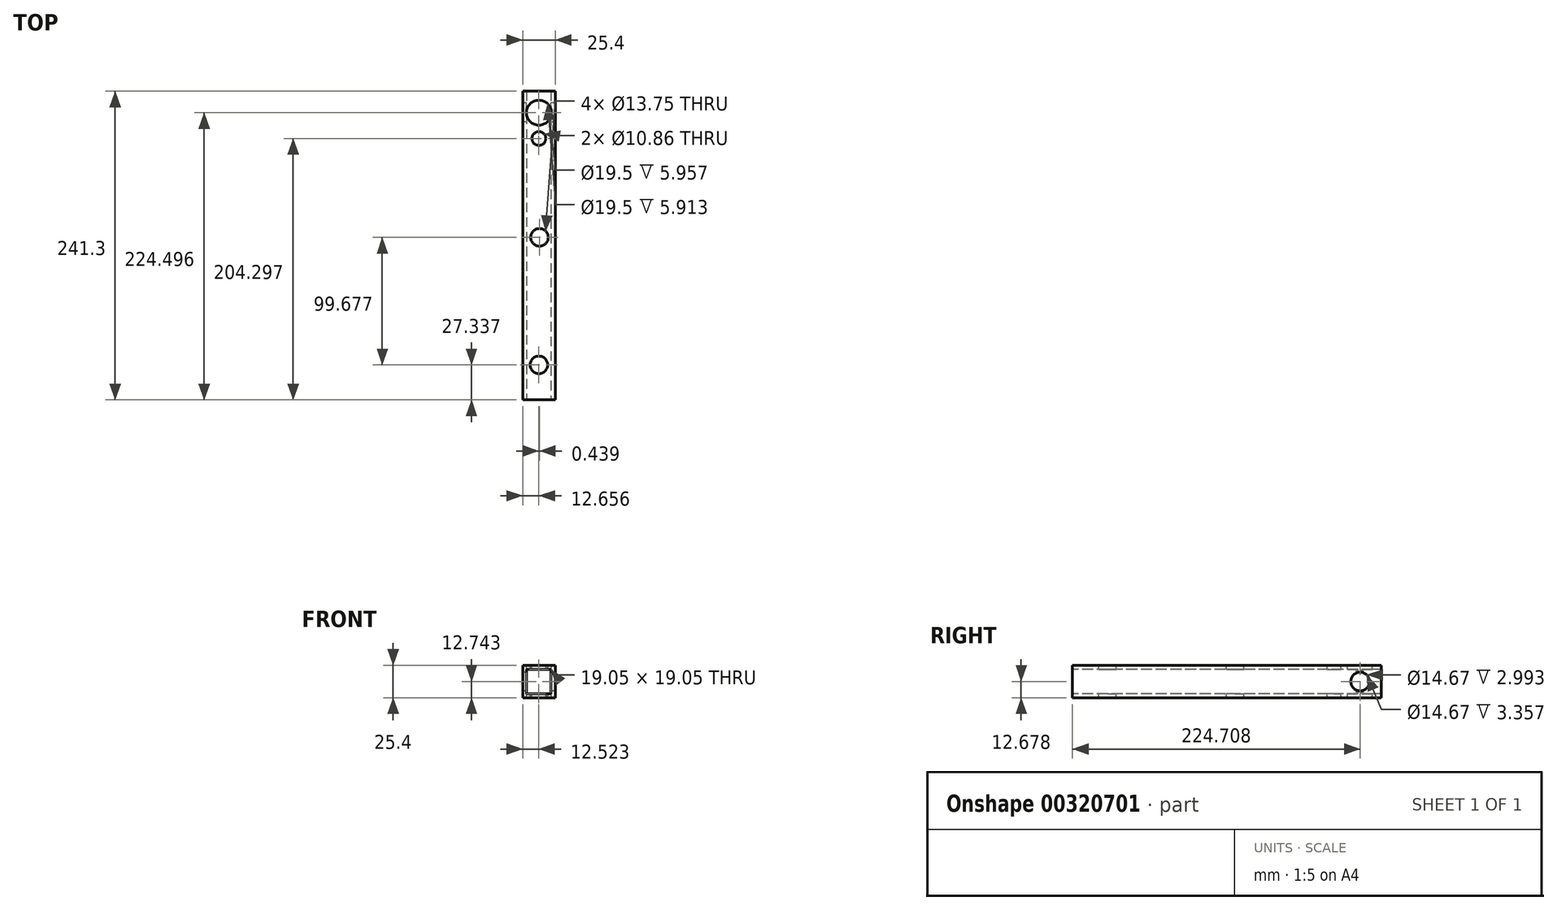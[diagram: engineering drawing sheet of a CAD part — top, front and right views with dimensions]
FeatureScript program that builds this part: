
annotation { "Feature Type Name" : "Feature", "Feature Type Description" : "" }
export const myFeature = defineFeature(function(context is Context, id is Id, definition is map)
    precondition{}
    {
        {
            var Q0;
            Q0=qCreatedBy(makeId("Top.planeOp"),FACE);
            var sketch = newSketch(context, id + "F0", { "sketchPlane" : qUnion([Q0])});
            skLineSegment(sketch, "E0", {"start": v(-60.08, 121.67) * mm, "end": v(-60.08, -119.63) * mm});
            skLineSegment(sketch, "E1", {"start": v(-60.08, -119.63) * mm, "end": v(-34.68, -119.63) * mm});
            skLineSegment(sketch, "E2", {"start": v(-34.68, -119.63) * mm, "end": v(-34.68, 121.67) * mm});
            skLineSegment(sketch, "E3", {"start": v(-34.68, 121.67) * mm, "end": v(-60.08, 121.67) * mm});
            skSolve(sketch);
        }
        {
            var Q0;
            Q0=makeQuery(id+"F0.imprint","IMPRINT",FACE,{"disambiguationData":[TD([[makeQuery(id+"F0.imprint","IMPRINT",EDGE,{"derivedFrom":sQuery(id+"F0.wireOp",EDGE,"E0")}),1.0]])]});
            extrude(context, id + "F1", {"entities" : qUnion([Q0]), "depth" : 25.4 * mm});
        }
        {
            var Q0;
            Q0=makeQuery(id+"F1.opExtrude","SWEPT_FACE",FACE,{"disambiguationData":[OSD([sQuery(id+"F0.wireOp",EDGE,"E1")])]});
            var sketch = newSketch(context, id + "F2", { "sketchPlane" : qUnion([Q0])});
            skLineSegment(sketch, "E4", {"start": v(-57.08, 22.27) * mm, "end": v(-57.08, 3.22) * mm});
            skLineSegment(sketch, "E5", {"start": v(-57.08, 3.22) * mm, "end": v(-38.03, 3.22) * mm});
            skLineSegment(sketch, "E6", {"start": v(-38.03, 3.22) * mm, "end": v(-38.03, 22.27) * mm});
            skLineSegment(sketch, "E7", {"start": v(-38.03, 22.27) * mm, "end": v(-57.08, 22.27) * mm});
            skSolve(sketch);
        }
        {
            var Q0;
            Q0=qSketchRegion(id+"F2",true);
            extrude(context, id + "F3", {"entities" : qUnion([Q0]), "operationType" : NewBodyOperationType.REMOVE, "oppositeDirection" : true, "depth" : 277.64 * mm});
        }
        {
            var Q0;
            Q0=makeQuery(id+"F1.opExtrude","CAP_FACE",FACE,{"disambiguationData":[OSD([sQuery(id+"F0.wireOp",EDGE,"E0"),sQuery(id+"F0.wireOp",EDGE,"E1"),sQuery(id+"F0.wireOp",EDGE,"E2"),sQuery(id+"F0.wireOp",EDGE,"E3")])],"isStart":false});
            var sketch = newSketch(context, id + "F4", { "sketchPlane" : qUnion([Q0])});
            skCircle(sketch, "E8", {"center": v(-47.42, 104.87) * mm, "radius": 9.75 * mm});
            skCircle(sketch, "E9", {"center": v(-47.42, 84.67) * mm, "radius": 5.43 * mm});
            skCircle(sketch, "E10", {"center": v(-46.98, 7.38) * mm, "radius": 6.87 * mm});
            skCircle(sketch, "E11", {"center": v(-47.42, -92.3) * mm, "radius": 6.87 * mm});
            skSolve(sketch);
        }
        {
            var Q0;
            Q0=qSketchRegion(id+"F4",true);
            extrude(context, id + "F5", {"entities" : qUnion([Q0]), "operationType" : NewBodyOperationType.REMOVE, "oppositeDirection" : true, "depth" : 72.47 * mm});
        }
        {
            var Q0;
            Q0=makeQuery(id+"F1.opExtrude","SWEPT_FACE",FACE,{"disambiguationData":[OSD([sQuery(id+"F0.wireOp",EDGE,"E0")])]});
            var sketch = newSketch(context, id + "F6", { "sketchPlane" : qUnion([Q0])});
            skCircle(sketch, "E12", {"center": v(-105.08, 12.68) * mm, "radius": 7.33 * mm});
            skSolve(sketch);
        }
        {
            var Q0;
            Q0=qSketchRegion(id+"F6",true);
            extrude(context, id + "F7", {"entities" : qUnion([Q0]), "operationType" : NewBodyOperationType.REMOVE, "oppositeDirection" : true, "depth" : 90.9 * mm});
        }
    });
